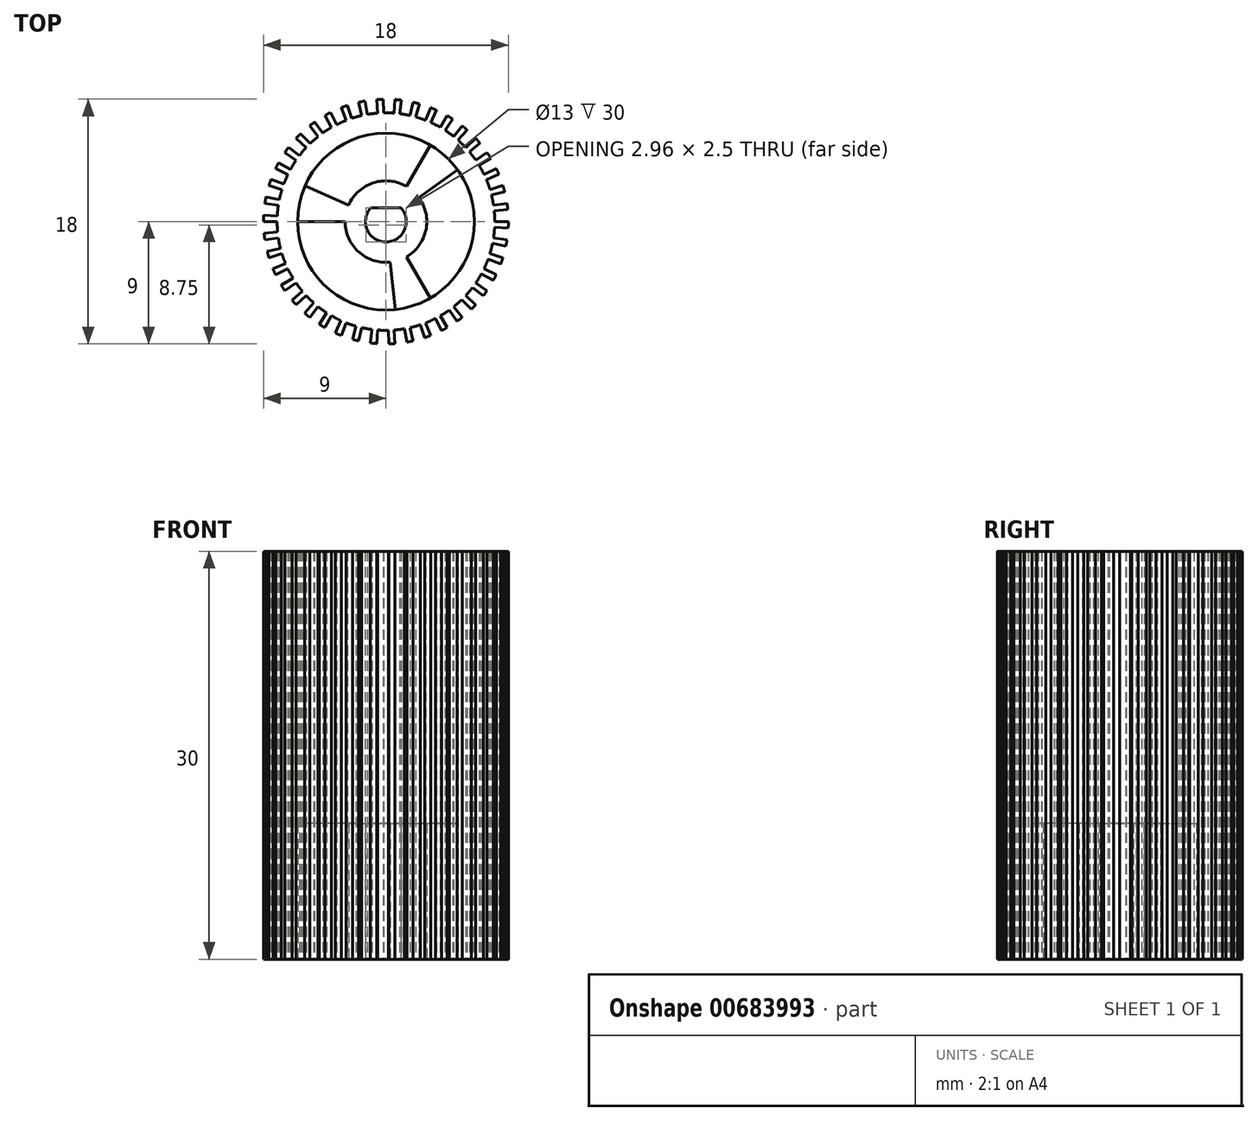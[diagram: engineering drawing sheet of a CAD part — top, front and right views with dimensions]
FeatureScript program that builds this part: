
annotation { "Feature Type Name" : "Feature", "Feature Type Description" : "" }
export const myFeature = defineFeature(function(context is Context, id is Id, definition is map)
    precondition{}
    {
        {
            var Q0;
            Q0=qCreatedBy(makeId("Top.planeOp"),FACE);
            var sketch = newSketch(context, id + "F0", { "sketchPlane" : qUnion([Q0])});
            skCircle(sketch, "E0", {"center": v(0, 0) * mm, "radius": 6.5 * mm});
            skCircle(sketch, "E1.0", {"center": v(0, 0) * mm, "radius": 8 * mm});
            skArc(sketch, "E2.0", {"start": v(-8.99, 0.47) * mm, "mid": v(-9, 0.24) * mm, "end": v(-9, 0) * mm});
            skLineSegment(sketch, "E3.trimOffspring", {"start": v(-7.99, 0.42) * mm, "end": v(-8.99, 0.47) * mm});
            skLineSegment(sketch, "E4.trimOffspring", {"start": v(-8, 0) * mm, "end": v(-9, 0) * mm});
            skLineSegment(sketch, "E5.1.0", {"start": v(-7.96, -0.78) * mm, "end": v(-8.96, -0.87) * mm});
            skLineSegment(sketch, "E5.1.1", {"start": v(-7.91, -1.2) * mm, "end": v(-8.9, -1.34) * mm});
            skArc(sketch, "E5.1.2", {"start": v(-8.96, -0.87) * mm, "mid": v(-8.93, -1.1) * mm, "end": v(-8.9, -1.34) * mm});
            skLineSegment(sketch, "E5.2.0", {"start": v(-7.76, -1.95) * mm, "end": v(-8.73, -2.2) * mm});
            skLineSegment(sketch, "E5.2.1", {"start": v(-7.64, -2.36) * mm, "end": v(-8.6, -2.65) * mm});
            skArc(sketch, "E5.2.2", {"start": v(-8.73, -2.2) * mm, "mid": v(-8.67, -2.43) * mm, "end": v(-8.6, -2.65) * mm});
            skLineSegment(sketch, "E5.3.0", {"start": v(-7.38, -3.09) * mm, "end": v(-8.3, -3.48) * mm});
            skLineSegment(sketch, "E5.3.1", {"start": v(-7.2, -3.47) * mm, "end": v(-8.1, -3.9) * mm});
            skArc(sketch, "E5.3.2", {"start": v(-8.3, -3.48) * mm, "mid": v(-8.2, -3.7) * mm, "end": v(-8.1, -3.9) * mm});
            skLineSegment(sketch, "E5.4.0", {"start": v(-6.84, -4.15) * mm, "end": v(-7.7, -4.67) * mm});
            skLineSegment(sketch, "E5.4.1", {"start": v(-6.6, -4.5) * mm, "end": v(-7.44, -5.07) * mm});
            skArc(sketch, "E5.4.2", {"start": v(-7.7, -4.67) * mm, "mid": v(-7.57, -4.87) * mm, "end": v(-7.44, -5.07) * mm});
            skLineSegment(sketch, "E5.5.0", {"start": v(-6.14, -5.13) * mm, "end": v(-6.9, -5.77) * mm});
            skLineSegment(sketch, "E5.5.1", {"start": v(-5.86, -5.44) * mm, "end": v(-6.6, -6.12) * mm});
            skArc(sketch, "E5.5.2", {"start": v(-6.9, -5.77) * mm, "mid": v(-6.76, -5.95) * mm, "end": v(-6.6, -6.12) * mm});
            skLineSegment(sketch, "E5.6.0", {"start": v(-5.3, -5.99) * mm, "end": v(-5.97, -6.73) * mm});
            skLineSegment(sketch, "E5.6.1", {"start": v(-4.99, -6.25) * mm, "end": v(-5.61, -7.04) * mm});
            skArc(sketch, "E5.6.2", {"start": v(-5.97, -6.73) * mm, "mid": v(-5.8, -6.89) * mm, "end": v(-5.61, -7.04) * mm});
            skLineSegment(sketch, "E5.7.0", {"start": v(-4.36, -6.7) * mm, "end": v(-4.9, -7.55) * mm});
            skLineSegment(sketch, "E5.7.1", {"start": v(-4, -6.93) * mm, "end": v(-4.5, -7.8) * mm});
            skArc(sketch, "E5.7.2", {"start": v(-4.9, -7.55) * mm, "mid": v(-4.7, -7.67) * mm, "end": v(-4.5, -7.8) * mm});
            skLineSegment(sketch, "E5.8.0", {"start": v(-3.3, -7.28) * mm, "end": v(-3.72, -8.2) * mm});
            skLineSegment(sketch, "E5.8.1", {"start": v(-2.92, -7.45) * mm, "end": v(-3.29, -8.38) * mm});
            skArc(sketch, "E5.8.2", {"start": v(-3.72, -8.2) * mm, "mid": v(-3.5, -8.29) * mm, "end": v(-3.29, -8.38) * mm});
            skLineSegment(sketch, "E5.9.0", {"start": v(-2.19, -7.7) * mm, "end": v(-2.46, -8.66) * mm});
            skLineSegment(sketch, "E5.9.1", {"start": v(-1.78, -7.8) * mm, "end": v(-2, -8.77) * mm});
            skArc(sketch, "E5.9.2", {"start": v(-2.46, -8.66) * mm, "mid": v(-2.23, -8.72) * mm, "end": v(-2, -8.77) * mm});
            skLineSegment(sketch, "E5.10.0", {"start": v(-1.01, -7.94) * mm, "end": v(-1.14, -8.93) * mm});
            skLineSegment(sketch, "E5.10.1", {"start": v(-0.6, -7.98) * mm, "end": v(-0.67, -8.97) * mm});
            skArc(sketch, "E5.10.2", {"start": v(-1.14, -8.93) * mm, "mid": v(-0.9, -8.95) * mm, "end": v(-0.67, -8.97) * mm});
            skLineSegment(sketch, "E5.11.0", {"start": v(0.18, -8) * mm, "end": v(0.2, -9) * mm});
            skLineSegment(sketch, "E5.11.1", {"start": v(0.6, -7.98) * mm, "end": v(0.67, -8.97) * mm});
            skArc(sketch, "E5.11.2", {"start": v(0.2, -9) * mm, "mid": v(0.44, -8.99) * mm, "end": v(0.67, -8.97) * mm});
            skLineSegment(sketch, "E5.12.0", {"start": v(1.37, -7.88) * mm, "end": v(1.54, -8.87) * mm});
            skLineSegment(sketch, "E5.12.1", {"start": v(1.78, -7.8) * mm, "end": v(2, -8.77) * mm});
            skArc(sketch, "E5.12.2", {"start": v(1.54, -8.87) * mm, "mid": v(1.77, -8.82) * mm, "end": v(2, -8.77) * mm});
            skLineSegment(sketch, "E5.13.0", {"start": v(2.53, -7.59) * mm, "end": v(2.85, -8.54) * mm});
            skLineSegment(sketch, "E5.13.1", {"start": v(2.92, -7.45) * mm, "end": v(3.29, -8.38) * mm});
            skArc(sketch, "E5.13.2", {"start": v(2.85, -8.54) * mm, "mid": v(3.07, -8.46) * mm, "end": v(3.29, -8.38) * mm});
            skLineSegment(sketch, "E5.14.0", {"start": v(3.63, -7.13) * mm, "end": v(4.09, -8.02) * mm});
            skLineSegment(sketch, "E5.14.1", {"start": v(4, -6.93) * mm, "end": v(4.5, -7.8) * mm});
            skArc(sketch, "E5.14.2", {"start": v(4.09, -8.02) * mm, "mid": v(4.3, -7.9) * mm, "end": v(4.5, -7.8) * mm});
            skLineSegment(sketch, "E5.15.0", {"start": v(4.65, -6.5) * mm, "end": v(5.24, -7.32) * mm});
            skLineSegment(sketch, "E5.15.1", {"start": v(4.99, -6.25) * mm, "end": v(5.61, -7.04) * mm});
            skArc(sketch, "E5.15.2", {"start": v(5.24, -7.32) * mm, "mid": v(5.43, -7.18) * mm, "end": v(5.61, -7.04) * mm});
            skLineSegment(sketch, "E5.16.0", {"start": v(5.57, -5.74) * mm, "end": v(6.27, -6.46) * mm});
            skLineSegment(sketch, "E5.16.1", {"start": v(5.86, -5.44) * mm, "end": v(6.6, -6.12) * mm});
            skArc(sketch, "E5.16.2", {"start": v(6.27, -6.46) * mm, "mid": v(6.43, -6.3) * mm, "end": v(6.6, -6.12) * mm});
            skLineSegment(sketch, "E5.17.0", {"start": v(6.36, -4.85) * mm, "end": v(7.16, -5.45) * mm});
            skLineSegment(sketch, "E5.17.1", {"start": v(6.6, -4.5) * mm, "end": v(7.44, -5.07) * mm});
            skArc(sketch, "E5.17.2", {"start": v(7.16, -5.45) * mm, "mid": v(7.3, -5.26) * mm, "end": v(7.44, -5.07) * mm});
            skLineSegment(sketch, "E5.18.0", {"start": v(7.02, -3.84) * mm, "end": v(7.9, -4.32) * mm});
            skLineSegment(sketch, "E5.18.1", {"start": v(7.2, -3.47) * mm, "end": v(8.1, -3.9) * mm});
            skArc(sketch, "E5.18.2", {"start": v(7.9, -4.32) * mm, "mid": v(8, -4.12) * mm, "end": v(8.1, -3.9) * mm});
            skLineSegment(sketch, "E5.19.0", {"start": v(7.51, -2.75) * mm, "end": v(8.45, -3.1) * mm});
            skLineSegment(sketch, "E5.19.1", {"start": v(7.64, -2.36) * mm, "end": v(8.6, -2.65) * mm});
            skArc(sketch, "E5.19.2", {"start": v(8.45, -3.1) * mm, "mid": v(8.53, -2.88) * mm, "end": v(8.6, -2.65) * mm});
            skLineSegment(sketch, "E5.20.0", {"start": v(7.84, -1.6) * mm, "end": v(8.82, -1.8) * mm});
            skLineSegment(sketch, "E5.20.1", {"start": v(7.91, -1.2) * mm, "end": v(8.9, -1.34) * mm});
            skArc(sketch, "E5.20.2", {"start": v(8.82, -1.8) * mm, "mid": v(8.86, -1.57) * mm, "end": v(8.9, -1.34) * mm});
            skLineSegment(sketch, "E5.21.0", {"start": v(7.99, -0.42) * mm, "end": v(8.99, -0.47) * mm});
            skLineSegment(sketch, "E5.21.1", {"start": v(8, 0) * mm, "end": v(9, 0) * mm});
            skArc(sketch, "E5.21.2", {"start": v(8.99, -0.47) * mm, "mid": v(9, -0.24) * mm, "end": v(9, 0) * mm});
            skLineSegment(sketch, "E5.22.0", {"start": v(7.96, 0.78) * mm, "end": v(8.96, 0.87) * mm});
            skLineSegment(sketch, "E5.22.1", {"start": v(7.91, 1.2) * mm, "end": v(8.9, 1.34) * mm});
            skArc(sketch, "E5.22.2", {"start": v(8.96, 0.87) * mm, "mid": v(8.93, 1.1) * mm, "end": v(8.9, 1.34) * mm});
            skLineSegment(sketch, "E5.23.0", {"start": v(7.76, 1.95) * mm, "end": v(8.73, 2.2) * mm});
            skLineSegment(sketch, "E5.23.1", {"start": v(7.64, 2.36) * mm, "end": v(8.6, 2.65) * mm});
            skArc(sketch, "E5.23.2", {"start": v(8.73, 2.2) * mm, "mid": v(8.67, 2.43) * mm, "end": v(8.6, 2.65) * mm});
            skLineSegment(sketch, "E5.24.0", {"start": v(7.38, 3.09) * mm, "end": v(8.3, 3.48) * mm});
            skLineSegment(sketch, "E5.24.1", {"start": v(7.2, 3.47) * mm, "end": v(8.1, 3.9) * mm});
            skArc(sketch, "E5.24.2", {"start": v(8.3, 3.48) * mm, "mid": v(8.2, 3.7) * mm, "end": v(8.1, 3.9) * mm});
            skLineSegment(sketch, "E5.25.0", {"start": v(6.84, 4.15) * mm, "end": v(7.7, 4.67) * mm});
            skLineSegment(sketch, "E5.25.1", {"start": v(6.6, 4.5) * mm, "end": v(7.44, 5.07) * mm});
            skArc(sketch, "E5.25.2", {"start": v(7.7, 4.67) * mm, "mid": v(7.57, 4.87) * mm, "end": v(7.44, 5.07) * mm});
            skLineSegment(sketch, "E5.26.0", {"start": v(6.14, 5.13) * mm, "end": v(6.9, 5.77) * mm});
            skLineSegment(sketch, "E5.26.1", {"start": v(5.86, 5.44) * mm, "end": v(6.6, 6.12) * mm});
            skArc(sketch, "E5.26.2", {"start": v(6.9, 5.77) * mm, "mid": v(6.76, 5.95) * mm, "end": v(6.6, 6.12) * mm});
            skLineSegment(sketch, "E5.27.0", {"start": v(5.3, 5.99) * mm, "end": v(5.97, 6.73) * mm});
            skLineSegment(sketch, "E5.27.1", {"start": v(4.99, 6.25) * mm, "end": v(5.61, 7.04) * mm});
            skArc(sketch, "E5.27.2", {"start": v(5.97, 6.73) * mm, "mid": v(5.8, 6.89) * mm, "end": v(5.61, 7.04) * mm});
            skLineSegment(sketch, "E5.28.0", {"start": v(4.36, 6.7) * mm, "end": v(4.9, 7.55) * mm});
            skLineSegment(sketch, "E5.28.1", {"start": v(4, 6.93) * mm, "end": v(4.5, 7.8) * mm});
            skArc(sketch, "E5.28.2", {"start": v(4.9, 7.55) * mm, "mid": v(4.7, 7.67) * mm, "end": v(4.5, 7.8) * mm});
            skLineSegment(sketch, "E5.29.0", {"start": v(3.3, 7.28) * mm, "end": v(3.72, 8.2) * mm});
            skLineSegment(sketch, "E5.29.1", {"start": v(2.92, 7.45) * mm, "end": v(3.29, 8.38) * mm});
            skArc(sketch, "E5.29.2", {"start": v(3.72, 8.2) * mm, "mid": v(3.5, 8.29) * mm, "end": v(3.29, 8.38) * mm});
            skLineSegment(sketch, "E5.30.0", {"start": v(2.19, 7.7) * mm, "end": v(2.46, 8.66) * mm});
            skLineSegment(sketch, "E5.30.1", {"start": v(1.78, 7.8) * mm, "end": v(2, 8.77) * mm});
            skArc(sketch, "E5.30.2", {"start": v(2.46, 8.66) * mm, "mid": v(2.23, 8.72) * mm, "end": v(2, 8.77) * mm});
            skLineSegment(sketch, "E5.31.0", {"start": v(1.01, 7.94) * mm, "end": v(1.14, 8.93) * mm});
            skLineSegment(sketch, "E5.31.1", {"start": v(0.6, 7.98) * mm, "end": v(0.67, 8.97) * mm});
            skArc(sketch, "E5.31.2", {"start": v(1.14, 8.93) * mm, "mid": v(0.9, 8.95) * mm, "end": v(0.67, 8.97) * mm});
            skLineSegment(sketch, "E5.32.0", {"start": v(-0.18, 8) * mm, "end": v(-0.2, 9) * mm});
            skLineSegment(sketch, "E5.32.1", {"start": v(-0.6, 7.98) * mm, "end": v(-0.67, 8.97) * mm});
            skArc(sketch, "E5.32.2", {"start": v(-0.2, 9) * mm, "mid": v(-0.44, 8.99) * mm, "end": v(-0.67, 8.97) * mm});
            skLineSegment(sketch, "E5.33.0", {"start": v(-1.37, 7.88) * mm, "end": v(-1.54, 8.87) * mm});
            skLineSegment(sketch, "E5.33.1", {"start": v(-1.78, 7.8) * mm, "end": v(-2, 8.77) * mm});
            skArc(sketch, "E5.33.2", {"start": v(-1.54, 8.87) * mm, "mid": v(-1.77, 8.82) * mm, "end": v(-2, 8.77) * mm});
            skLineSegment(sketch, "E5.34.0", {"start": v(-2.53, 7.59) * mm, "end": v(-2.85, 8.54) * mm});
            skLineSegment(sketch, "E5.34.1", {"start": v(-2.92, 7.45) * mm, "end": v(-3.29, 8.38) * mm});
            skArc(sketch, "E5.34.2", {"start": v(-2.85, 8.54) * mm, "mid": v(-3.07, 8.46) * mm, "end": v(-3.29, 8.38) * mm});
            skLineSegment(sketch, "E5.35.0", {"start": v(-3.63, 7.13) * mm, "end": v(-4.09, 8.02) * mm});
            skLineSegment(sketch, "E5.35.1", {"start": v(-4, 6.93) * mm, "end": v(-4.5, 7.8) * mm});
            skArc(sketch, "E5.35.2", {"start": v(-4.09, 8.02) * mm, "mid": v(-4.3, 7.9) * mm, "end": v(-4.5, 7.8) * mm});
            skLineSegment(sketch, "E5.36.0", {"start": v(-4.65, 6.5) * mm, "end": v(-5.24, 7.32) * mm});
            skLineSegment(sketch, "E5.36.1", {"start": v(-4.99, 6.25) * mm, "end": v(-5.61, 7.04) * mm});
            skArc(sketch, "E5.36.2", {"start": v(-5.24, 7.32) * mm, "mid": v(-5.43, 7.18) * mm, "end": v(-5.61, 7.04) * mm});
            skLineSegment(sketch, "E5.37.0", {"start": v(-5.57, 5.74) * mm, "end": v(-6.27, 6.46) * mm});
            skLineSegment(sketch, "E5.37.1", {"start": v(-5.86, 5.44) * mm, "end": v(-6.6, 6.12) * mm});
            skArc(sketch, "E5.37.2", {"start": v(-6.27, 6.46) * mm, "mid": v(-6.43, 6.3) * mm, "end": v(-6.6, 6.12) * mm});
            skLineSegment(sketch, "E5.38.0", {"start": v(-6.36, 4.85) * mm, "end": v(-7.16, 5.45) * mm});
            skLineSegment(sketch, "E5.38.1", {"start": v(-6.6, 4.5) * mm, "end": v(-7.44, 5.07) * mm});
            skArc(sketch, "E5.38.2", {"start": v(-7.16, 5.45) * mm, "mid": v(-7.3, 5.26) * mm, "end": v(-7.44, 5.07) * mm});
            skLineSegment(sketch, "E5.39.0", {"start": v(-7.02, 3.84) * mm, "end": v(-7.9, 4.32) * mm});
            skLineSegment(sketch, "E5.39.1", {"start": v(-7.2, 3.47) * mm, "end": v(-8.1, 3.9) * mm});
            skArc(sketch, "E5.39.2", {"start": v(-7.9, 4.32) * mm, "mid": v(-8, 4.12) * mm, "end": v(-8.1, 3.9) * mm});
            skLineSegment(sketch, "E5.40.0", {"start": v(-7.51, 2.75) * mm, "end": v(-8.45, 3.1) * mm});
            skLineSegment(sketch, "E5.40.1", {"start": v(-7.64, 2.36) * mm, "end": v(-8.6, 2.65) * mm});
            skArc(sketch, "E5.40.2", {"start": v(-8.45, 3.1) * mm, "mid": v(-8.53, 2.88) * mm, "end": v(-8.6, 2.65) * mm});
            skLineSegment(sketch, "E5.41.0", {"start": v(-7.84, 1.6) * mm, "end": v(-8.82, 1.8) * mm});
            skLineSegment(sketch, "E5.41.1", {"start": v(-7.91, 1.2) * mm, "end": v(-8.9, 1.34) * mm});
            skArc(sketch, "E5.41.2", {"start": v(-8.82, 1.8) * mm, "mid": v(-8.86, 1.57) * mm, "end": v(-8.9, 1.34) * mm});
            skArc(sketch, "E6", {"start": v(-1.12, 1) * mm, "mid": v(0, -1.5) * mm, "end": v(1.12, 1) * mm});
            skLineSegment(sketch, "E7", {"start": v(-1.12, 1) * mm, "end": v(1.12, 1) * mm});
            skCircle(sketch, "E8.0", {"center": v(0, 0) * mm, "radius": 3 * mm});
            skLineSegment(sketch, "E9.trimOffspring", {"start": v(-2.74, 1.22) * mm, "end": v(-5.94, 2.64) * mm});
            skLineSegment(sketch, "E10.trimOffspring", {"start": v(-3, 0) * mm, "end": v(-6.5, 0) * mm});
            skLineSegment(sketch, "E11.1.0", {"start": v(0.31, -2.98) * mm, "end": v(0.68, -6.46) * mm});
            skLineSegment(sketch, "E11.1.1", {"start": v(1.5, -2.6) * mm, "end": v(3.25, -5.63) * mm});
            skLineSegment(sketch, "E11.2.0", {"start": v(2.43, 1.76) * mm, "end": v(5.26, 3.82) * mm});
            skLineSegment(sketch, "E11.2.1", {"start": v(1.5, 2.6) * mm, "end": v(3.25, 5.63) * mm});
            skSolve(sketch);
        }
        {
            var Q0;
            {var subQ0=sQuery(id+"F0.wireOp",EDGE,"E10.trimOffspring");Q0=makeQuery(id+"F0.imprint","IMPRINT",FACE,{"disambiguationData":[TD([[makeQuery(id+"F0.imprint","IMPRINT",EDGE,{"derivedFrom":subQ0}),1.0]])]});}
            var Q1;
            {var subQ0=sQuery(id+"F0.wireOp",EDGE,"E9.trimOffspring");Q1=makeQuery(id+"F0.imprint","IMPRINT",FACE,{"disambiguationData":[TD([[makeQuery(id+"F0.imprint","IMPRINT",EDGE,{"derivedFrom":subQ0}),1.0]])]});}
            var Q2;
            {var subQ0=sQuery(id+"F0.wireOp",EDGE,"E9.trimOffspring");Q2=makeQuery(id+"F0.imprint","IMPRINT",FACE,{"disambiguationData":[TD([[makeQuery(id+"F0.imprint","IMPRINT",EDGE,{"derivedFrom":subQ0}),-1.0]])]});}
            var Q3;
            {var subQ0=sQuery(id+"F0.wireOp",EDGE,"E11.2.0");Q3=makeQuery(id+"F0.imprint","IMPRINT",FACE,{"disambiguationData":[TD([[makeQuery(id+"F0.imprint","IMPRINT",EDGE,{"derivedFrom":subQ0}),1.0]])]});}
            var Q4;
            {var subQ0=sQuery(id+"F0.wireOp",EDGE,"E11.1.1");Q4=makeQuery(id+"F0.imprint","IMPRINT",FACE,{"disambiguationData":[TD([[makeQuery(id+"F0.imprint","IMPRINT",EDGE,{"derivedFrom":subQ0}),1.0]])]});}
            var Q5;
            {var subQ0=sQuery(id+"F0.wireOp",EDGE,"E11.1.0");Q5=makeQuery(id+"F0.imprint","IMPRINT",FACE,{"disambiguationData":[TD([[makeQuery(id+"F0.imprint","IMPRINT",EDGE,{"derivedFrom":subQ0}),1.0]])]});}
            extrude(context, id + "F1", {"entities" : qUnion([Q0, Q1, Q2, Q3, Q4, Q5]), "depth" : 1.5 * mm, "offsetDistance" : 25 * mm});
        }
        {
            var Q0;
            {var subQ31=sQuery(id+"F0.wireOp",EDGE,"E0");var subQ33=makeQuery(id+"F0.imprint","INTERSECT",VERTEX,{"derivedFrom":[subQ31,sQuery(id+"F0.wireOp",EDGE,"E11.2.0")]});Q0=makeQuery(id+"F0.imprint","IMPRINT",FACE,{"disambiguationData":[TD([[makeQuery(id+"F0.imprint","IMPRINT",EDGE,{"disambiguationData":[TD([[subQ33,-1.0]])],"derivedFrom":subQ31}),-1.0]])]});}
            var Q1;
            {var subQ0=sQuery(id+"F0.wireOp",EDGE,"E5.38.0");Q1=makeQuery(id+"F0.imprint","IMPRINT",FACE,{"disambiguationData":[TD([[makeQuery(id+"F0.imprint","IMPRINT",EDGE,{"derivedFrom":subQ0}),1.0]])]});}
            var Q2;
            {var subQ0=sQuery(id+"F0.wireOp",EDGE,"E5.37.0");Q2=makeQuery(id+"F0.imprint","IMPRINT",FACE,{"disambiguationData":[TD([[makeQuery(id+"F0.imprint","IMPRINT",EDGE,{"derivedFrom":subQ0}),1.0]])]});}
            var Q3;
            {var subQ0=sQuery(id+"F0.wireOp",EDGE,"E5.36.0");Q3=makeQuery(id+"F0.imprint","IMPRINT",FACE,{"disambiguationData":[TD([[makeQuery(id+"F0.imprint","IMPRINT",EDGE,{"derivedFrom":subQ0}),1.0]])]});}
            var Q4;
            {var subQ0=sQuery(id+"F0.wireOp",EDGE,"E5.35.0");Q4=makeQuery(id+"F0.imprint","IMPRINT",FACE,{"disambiguationData":[TD([[makeQuery(id+"F0.imprint","IMPRINT",EDGE,{"derivedFrom":subQ0}),1.0]])]});}
            var Q5;
            {var subQ0=sQuery(id+"F0.wireOp",EDGE,"E5.34.0");Q5=makeQuery(id+"F0.imprint","IMPRINT",FACE,{"disambiguationData":[TD([[makeQuery(id+"F0.imprint","IMPRINT",EDGE,{"derivedFrom":subQ0}),1.0]])]});}
            var Q6;
            {var subQ0=sQuery(id+"F0.wireOp",EDGE,"E5.33.0");Q6=makeQuery(id+"F0.imprint","IMPRINT",FACE,{"disambiguationData":[TD([[makeQuery(id+"F0.imprint","IMPRINT",EDGE,{"derivedFrom":subQ0}),1.0]])]});}
            var Q7;
            {var subQ0=sQuery(id+"F0.wireOp",EDGE,"E5.32.0");Q7=makeQuery(id+"F0.imprint","IMPRINT",FACE,{"disambiguationData":[TD([[makeQuery(id+"F0.imprint","IMPRINT",EDGE,{"derivedFrom":subQ0}),1.0]])]});}
            var Q8;
            {var subQ0=sQuery(id+"F0.wireOp",EDGE,"E5.31.0");Q8=makeQuery(id+"F0.imprint","IMPRINT",FACE,{"disambiguationData":[TD([[makeQuery(id+"F0.imprint","IMPRINT",EDGE,{"derivedFrom":subQ0}),1.0]])]});}
            var Q9;
            {var subQ0=sQuery(id+"F0.wireOp",EDGE,"E5.30.0");Q9=makeQuery(id+"F0.imprint","IMPRINT",FACE,{"disambiguationData":[TD([[makeQuery(id+"F0.imprint","IMPRINT",EDGE,{"derivedFrom":subQ0}),1.0]])]});}
            var Q10;
            {var subQ0=sQuery(id+"F0.wireOp",EDGE,"E5.29.0");Q10=makeQuery(id+"F0.imprint","IMPRINT",FACE,{"disambiguationData":[TD([[makeQuery(id+"F0.imprint","IMPRINT",EDGE,{"derivedFrom":subQ0}),1.0]])]});}
            var Q11;
            {var subQ0=sQuery(id+"F0.wireOp",EDGE,"E5.28.0");Q11=makeQuery(id+"F0.imprint","IMPRINT",FACE,{"disambiguationData":[TD([[makeQuery(id+"F0.imprint","IMPRINT",EDGE,{"derivedFrom":subQ0}),1.0]])]});}
            var Q12;
            {var subQ0=sQuery(id+"F0.wireOp",EDGE,"E5.27.0");Q12=makeQuery(id+"F0.imprint","IMPRINT",FACE,{"disambiguationData":[TD([[makeQuery(id+"F0.imprint","IMPRINT",EDGE,{"derivedFrom":subQ0}),1.0]])]});}
            var Q13;
            {var subQ0=sQuery(id+"F0.wireOp",EDGE,"E5.26.0");Q13=makeQuery(id+"F0.imprint","IMPRINT",FACE,{"disambiguationData":[TD([[makeQuery(id+"F0.imprint","IMPRINT",EDGE,{"derivedFrom":subQ0}),1.0]])]});}
            var Q14;
            {var subQ0=sQuery(id+"F0.wireOp",EDGE,"E5.25.0");Q14=makeQuery(id+"F0.imprint","IMPRINT",FACE,{"disambiguationData":[TD([[makeQuery(id+"F0.imprint","IMPRINT",EDGE,{"derivedFrom":subQ0}),1.0]])]});}
            var Q15;
            {var subQ0=sQuery(id+"F0.wireOp",EDGE,"E5.24.0");Q15=makeQuery(id+"F0.imprint","IMPRINT",FACE,{"disambiguationData":[TD([[makeQuery(id+"F0.imprint","IMPRINT",EDGE,{"derivedFrom":subQ0}),1.0]])]});}
            var Q16;
            {var subQ0=sQuery(id+"F0.wireOp",EDGE,"E5.23.0");Q16=makeQuery(id+"F0.imprint","IMPRINT",FACE,{"disambiguationData":[TD([[makeQuery(id+"F0.imprint","IMPRINT",EDGE,{"derivedFrom":subQ0}),1.0]])]});}
            var Q17;
            {var subQ0=sQuery(id+"F0.wireOp",EDGE,"E5.22.0");Q17=makeQuery(id+"F0.imprint","IMPRINT",FACE,{"disambiguationData":[TD([[makeQuery(id+"F0.imprint","IMPRINT",EDGE,{"derivedFrom":subQ0}),1.0]])]});}
            var Q18;
            {var subQ0=sQuery(id+"F0.wireOp",EDGE,"E5.21.0");Q18=makeQuery(id+"F0.imprint","IMPRINT",FACE,{"disambiguationData":[TD([[makeQuery(id+"F0.imprint","IMPRINT",EDGE,{"derivedFrom":subQ0}),1.0]])]});}
            var Q19;
            {var subQ0=sQuery(id+"F0.wireOp",EDGE,"E5.20.0");Q19=makeQuery(id+"F0.imprint","IMPRINT",FACE,{"disambiguationData":[TD([[makeQuery(id+"F0.imprint","IMPRINT",EDGE,{"derivedFrom":subQ0}),1.0]])]});}
            var Q20;
            {var subQ0=sQuery(id+"F0.wireOp",EDGE,"E5.19.0");Q20=makeQuery(id+"F0.imprint","IMPRINT",FACE,{"disambiguationData":[TD([[makeQuery(id+"F0.imprint","IMPRINT",EDGE,{"derivedFrom":subQ0}),1.0]])]});}
            var Q21;
            {var subQ0=sQuery(id+"F0.wireOp",EDGE,"E5.18.0");Q21=makeQuery(id+"F0.imprint","IMPRINT",FACE,{"disambiguationData":[TD([[makeQuery(id+"F0.imprint","IMPRINT",EDGE,{"derivedFrom":subQ0}),1.0]])]});}
            var Q22;
            {var subQ0=sQuery(id+"F0.wireOp",EDGE,"E5.17.0");Q22=makeQuery(id+"F0.imprint","IMPRINT",FACE,{"disambiguationData":[TD([[makeQuery(id+"F0.imprint","IMPRINT",EDGE,{"derivedFrom":subQ0}),1.0]])]});}
            var Q23;
            {var subQ0=sQuery(id+"F0.wireOp",EDGE,"E5.16.0");Q23=makeQuery(id+"F0.imprint","IMPRINT",FACE,{"disambiguationData":[TD([[makeQuery(id+"F0.imprint","IMPRINT",EDGE,{"derivedFrom":subQ0}),1.0]])]});}
            var Q24;
            {var subQ0=sQuery(id+"F0.wireOp",EDGE,"E5.15.0");Q24=makeQuery(id+"F0.imprint","IMPRINT",FACE,{"disambiguationData":[TD([[makeQuery(id+"F0.imprint","IMPRINT",EDGE,{"derivedFrom":subQ0}),1.0]])]});}
            var Q25;
            {var subQ0=sQuery(id+"F0.wireOp",EDGE,"E5.14.0");Q25=makeQuery(id+"F0.imprint","IMPRINT",FACE,{"disambiguationData":[TD([[makeQuery(id+"F0.imprint","IMPRINT",EDGE,{"derivedFrom":subQ0}),1.0]])]});}
            var Q26;
            {var subQ0=sQuery(id+"F0.wireOp",EDGE,"E5.13.0");Q26=makeQuery(id+"F0.imprint","IMPRINT",FACE,{"disambiguationData":[TD([[makeQuery(id+"F0.imprint","IMPRINT",EDGE,{"derivedFrom":subQ0}),1.0]])]});}
            var Q27;
            {var subQ0=sQuery(id+"F0.wireOp",EDGE,"E5.12.0");Q27=makeQuery(id+"F0.imprint","IMPRINT",FACE,{"disambiguationData":[TD([[makeQuery(id+"F0.imprint","IMPRINT",EDGE,{"derivedFrom":subQ0}),1.0]])]});}
            var Q28;
            {var subQ0=sQuery(id+"F0.wireOp",EDGE,"E5.11.0");Q28=makeQuery(id+"F0.imprint","IMPRINT",FACE,{"disambiguationData":[TD([[makeQuery(id+"F0.imprint","IMPRINT",EDGE,{"derivedFrom":subQ0}),1.0]])]});}
            var Q29;
            {var subQ0=sQuery(id+"F0.wireOp",EDGE,"E5.10.0");Q29=makeQuery(id+"F0.imprint","IMPRINT",FACE,{"disambiguationData":[TD([[makeQuery(id+"F0.imprint","IMPRINT",EDGE,{"derivedFrom":subQ0}),1.0]])]});}
            var Q30;
            {var subQ0=sQuery(id+"F0.wireOp",EDGE,"E5.9.0");Q30=makeQuery(id+"F0.imprint","IMPRINT",FACE,{"disambiguationData":[TD([[makeQuery(id+"F0.imprint","IMPRINT",EDGE,{"derivedFrom":subQ0}),1.0]])]});}
            var Q31;
            {var subQ0=sQuery(id+"F0.wireOp",EDGE,"E5.8.0");Q31=makeQuery(id+"F0.imprint","IMPRINT",FACE,{"disambiguationData":[TD([[makeQuery(id+"F0.imprint","IMPRINT",EDGE,{"derivedFrom":subQ0}),1.0]])]});}
            var Q32;
            {var subQ0=sQuery(id+"F0.wireOp",EDGE,"E5.7.0");Q32=makeQuery(id+"F0.imprint","IMPRINT",FACE,{"disambiguationData":[TD([[makeQuery(id+"F0.imprint","IMPRINT",EDGE,{"derivedFrom":subQ0}),1.0]])]});}
            var Q33;
            {var subQ0=sQuery(id+"F0.wireOp",EDGE,"E5.6.0");Q33=makeQuery(id+"F0.imprint","IMPRINT",FACE,{"disambiguationData":[TD([[makeQuery(id+"F0.imprint","IMPRINT",EDGE,{"derivedFrom":subQ0}),1.0]])]});}
            var Q34;
            {var subQ0=sQuery(id+"F0.wireOp",EDGE,"E5.5.0");Q34=makeQuery(id+"F0.imprint","IMPRINT",FACE,{"disambiguationData":[TD([[makeQuery(id+"F0.imprint","IMPRINT",EDGE,{"derivedFrom":subQ0}),1.0]])]});}
            var Q35;
            {var subQ0=sQuery(id+"F0.wireOp",EDGE,"E5.4.0");Q35=makeQuery(id+"F0.imprint","IMPRINT",FACE,{"disambiguationData":[TD([[makeQuery(id+"F0.imprint","IMPRINT",EDGE,{"derivedFrom":subQ0}),1.0]])]});}
            var Q36;
            {var subQ0=sQuery(id+"F0.wireOp",EDGE,"E5.3.0");Q36=makeQuery(id+"F0.imprint","IMPRINT",FACE,{"disambiguationData":[TD([[makeQuery(id+"F0.imprint","IMPRINT",EDGE,{"derivedFrom":subQ0}),1.0]])]});}
            var Q37;
            {var subQ0=sQuery(id+"F0.wireOp",EDGE,"E5.2.0");Q37=makeQuery(id+"F0.imprint","IMPRINT",FACE,{"disambiguationData":[TD([[makeQuery(id+"F0.imprint","IMPRINT",EDGE,{"derivedFrom":subQ0}),1.0]])]});}
            var Q38;
            {var subQ0=sQuery(id+"F0.wireOp",EDGE,"E5.1.0");Q38=makeQuery(id+"F0.imprint","IMPRINT",FACE,{"disambiguationData":[TD([[makeQuery(id+"F0.imprint","IMPRINT",EDGE,{"derivedFrom":subQ0}),1.0]])]});}
            var Q39;
            Q39=makeQuery(id+"F0.imprint","IMPRINT",FACE,{"disambiguationData":[TD([[makeQuery(id+"F0.imprint","IMPRINT",EDGE,{"derivedFrom":sQuery(id+"F0.wireOp",EDGE,"E2.0")}),1.0]])]});
            var Q40;
            {var subQ0=sQuery(id+"F0.wireOp",EDGE,"E5.41.0");Q40=makeQuery(id+"F0.imprint","IMPRINT",FACE,{"disambiguationData":[TD([[makeQuery(id+"F0.imprint","IMPRINT",EDGE,{"derivedFrom":subQ0}),1.0]])]});}
            var Q41;
            {var subQ0=sQuery(id+"F0.wireOp",EDGE,"E5.40.0");Q41=makeQuery(id+"F0.imprint","IMPRINT",FACE,{"disambiguationData":[TD([[makeQuery(id+"F0.imprint","IMPRINT",EDGE,{"derivedFrom":subQ0}),1.0]])]});}
            var Q42;
            {var subQ0=sQuery(id+"F0.wireOp",EDGE,"E5.39.0");Q42=makeQuery(id+"F0.imprint","IMPRINT",FACE,{"disambiguationData":[TD([[makeQuery(id+"F0.imprint","IMPRINT",EDGE,{"derivedFrom":subQ0}),1.0]])]});}
            extrude(context, id + "F2", {"entities" : qUnion([Q0, Q1, Q2, Q3, Q4, Q5, Q6, Q7, Q8, Q9, Q10, Q11, Q12, Q13, Q14, Q15, Q16, Q17, Q18, Q19, Q20, Q21, Q22, Q23, Q24, Q25, Q26, Q27, Q28, Q29, Q30, Q31, Q32, Q33, Q34, Q35, Q36, Q37, Q38, Q39, Q40, Q41, Q42]), "operationType" : NewBodyOperationType.ADD, "depth" : 30 * mm, "offsetDistance" : 25 * mm});
        }
        {
            var Q0;
            Q0=makeQuery(id+"F0.imprint","IMPRINT",FACE,{"disambiguationData":[TD([[makeQuery(id+"F0.imprint","IMPRINT",EDGE,{"derivedFrom":sQuery(id+"F0.wireOp",EDGE,"E6")}),-1.0]])]});
            extrude(context, id + "F3", {"entities" : qUnion([Q0]), "operationType" : NewBodyOperationType.ADD, "depth" : 10 * mm, "offsetDistance" : 25 * mm});
        }
        {
            var Q0;
            {var subQ0=sQuery(id+"F0.wireOp",EDGE,"E9.trimOffspring");Q0=makeQuery(id+"F0.imprint","IMPRINT",FACE,{"disambiguationData":[TD([[makeQuery(id+"F0.imprint","IMPRINT",EDGE,{"derivedFrom":subQ0}),1.0]])]});}
            var Q1;
            {var subQ0=sQuery(id+"F0.wireOp",EDGE,"E11.2.0");Q1=makeQuery(id+"F0.imprint","IMPRINT",FACE,{"disambiguationData":[TD([[makeQuery(id+"F0.imprint","IMPRINT",EDGE,{"derivedFrom":subQ0}),1.0]])]});}
            var Q2;
            {var subQ0=sQuery(id+"F0.wireOp",EDGE,"E11.1.0");Q2=makeQuery(id+"F0.imprint","IMPRINT",FACE,{"disambiguationData":[TD([[makeQuery(id+"F0.imprint","IMPRINT",EDGE,{"derivedFrom":subQ0}),1.0]])]});}
            extrude(context, id + "F4", {"entities" : qUnion([Q0, Q1, Q2]), "operationType" : NewBodyOperationType.ADD, "depth" : 10 * mm, "offsetDistance" : 25 * mm});
        }
        {
            var Q0;
            {var subQ0=sQuery(id+"F0.wireOp",EDGE,"E11.1.1");Q0=makeQuery(id+"F0.imprint","IMPRINT",FACE,{"disambiguationData":[TD([[makeQuery(id+"F0.imprint","IMPRINT",EDGE,{"derivedFrom":subQ0}),1.0]])]});}
            var Q1;
            {var subQ0=sQuery(id+"F0.wireOp",EDGE,"E10.trimOffspring");Q1=makeQuery(id+"F0.imprint","IMPRINT",FACE,{"disambiguationData":[TD([[makeQuery(id+"F0.imprint","IMPRINT",EDGE,{"derivedFrom":subQ0}),1.0]])]});}
            var Q2;
            {var subQ0=sQuery(id+"F0.wireOp",EDGE,"E9.trimOffspring");Q2=makeQuery(id+"F0.imprint","IMPRINT",FACE,{"disambiguationData":[TD([[makeQuery(id+"F0.imprint","IMPRINT",EDGE,{"derivedFrom":subQ0}),-1.0]])]});}
            extrude(context, id + "F5", {"entities" : qUnion([Q0, Q1, Q2]), "operationType" : NewBodyOperationType.REMOVE, "oppositeDirection" : true, "depth" : -1.5 * mm, "offsetDistance" : 25 * mm});
        }
    });
